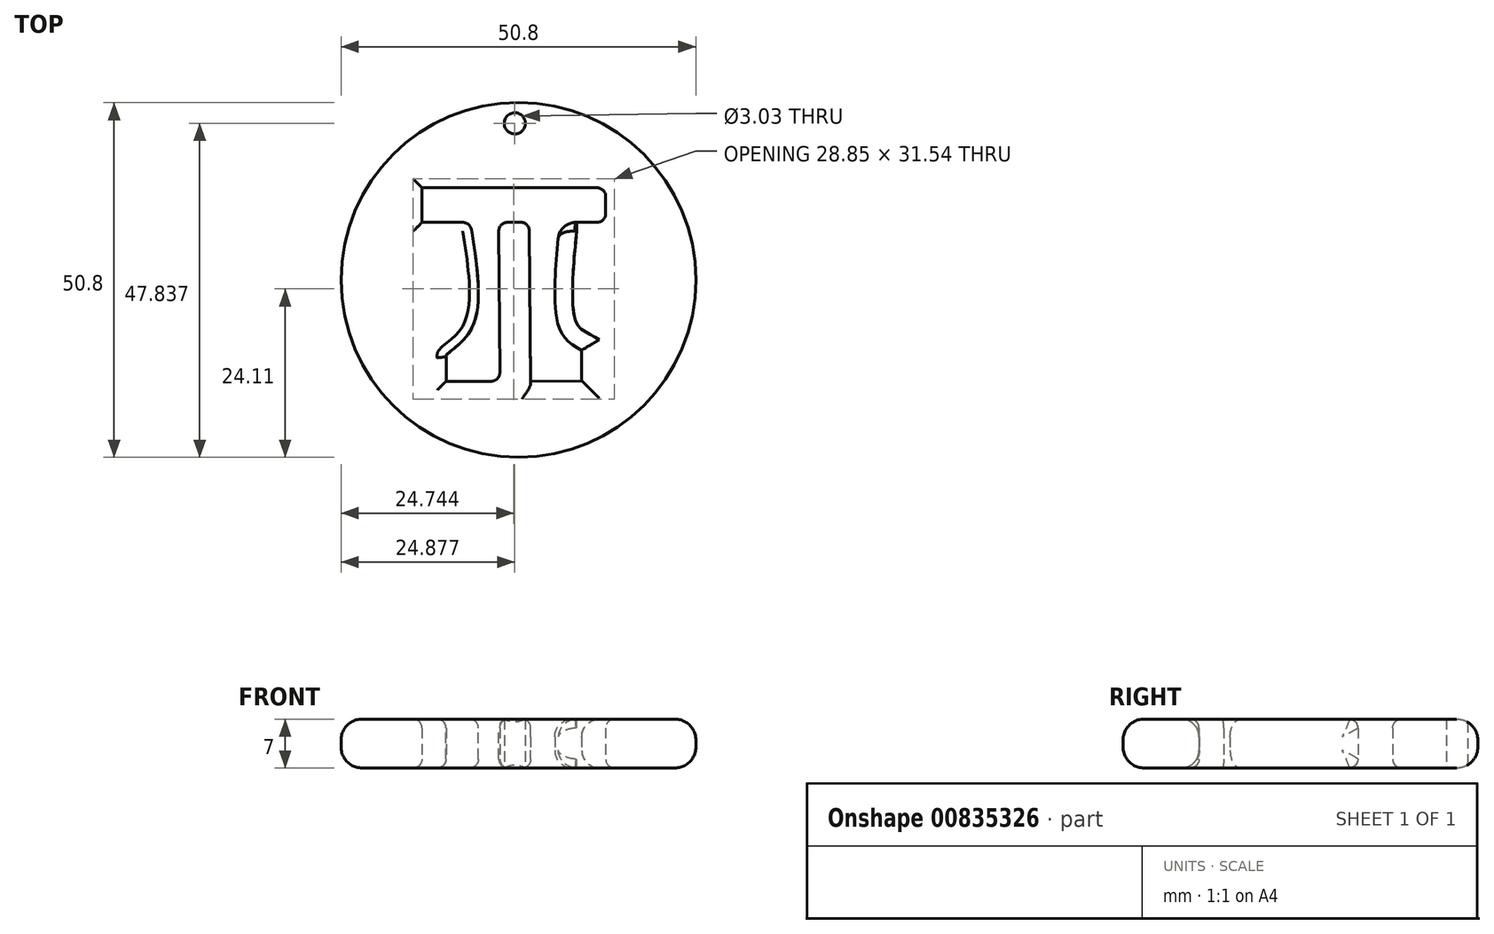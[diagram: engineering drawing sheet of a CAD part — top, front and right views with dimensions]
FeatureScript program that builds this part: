
annotation { "Feature Type Name" : "Feature", "Feature Type Description" : "" }
export const myFeature = defineFeature(function(context is Context, id is Id, definition is map)
    precondition{}
    {
        {
            var Q0;
            Q0=qCreatedBy(makeId("Top.planeOp"),FACE);
            var sketch = newSketch(context, id + "F0", { "sketchPlane" : qUnion([Q0])});
            skLineSegment(sketch, "E0", {"start": v(-26.31, 22.35) * mm, "end": v(0, 22.35) * mm});
            skLineSegment(sketch, "E1", {"start": v(0, 22.35) * mm, "end": v(0, 17.38) * mm});
            skLineSegment(sketch, "E2", {"start": v(0, 17.38) * mm, "end": v(-4.14, 17.38) * mm});
            skLineSegment(sketch, "E3", {"start": v(-26.31, 22.35) * mm, "end": v(-26.31, 17.38) * mm});
            skLineSegment(sketch, "E4", {"start": v(-26.31, 17.38) * mm, "end": v(-19.4, 17.38) * mm});
            skLineSegment(sketch, "E5", {"start": v(0, 17.38) * mm, "end": v(0, 19.87) * mm});
            skPoint(sketch, "E6.2.internal.snap0", {"position": v(-22.86, 17.38) * mm});
            skPoint(sketch, "E6.3.internal.snap0", {"position": v(-22.86, 17.38) * mm});
            skFitSpline(sketch, "E6", {"points": [v(-19.4, 17.38) * mm, v(-19.4, 1.83) * mm, v(-22.86, -1.63) * mm, v(-22.86, -1.83) * mm], "startDerivative": vector(5.13, -31.3) * mm, "endDerivative": vector(1.12, -2.6) * mm});
            skLineSegment(sketch, "E7", {"start": v(-22.86, -1.63) * mm, "end": v(-22.86, -5.37) * mm});
            skLineSegment(sketch, "E8", {"start": v(-22.86, -5.37) * mm, "end": v(-15.14, -5.37) * mm});
            skLineSegment(sketch, "E9", {"start": v(-15.34, 17.38) * mm, "end": v(-15.14, -5.37) * mm});
            skPoint(sketch, "E9.startSnap0", {"position": v(-2.07, 17.38) * mm});
            skLineSegment(sketch, "E10", {"start": v(-15.34, 17.38) * mm, "end": v(-10.94, 17.42) * mm});
            skLineSegment(sketch, "E11", {"start": v(-10.94, 17.42) * mm, "end": v(-10.75, -5.37) * mm});
            skCircle(sketch, "E12", {"center": v(-12.5, 9.14) * mm, "radius": 25.4 * mm});
            skCircle(sketch, "E13", {"center": v(-13.02, 31.58) * mm, "radius": 1.52 * mm});
            skCircle(sketch, "E14", {"center": v(-13.02, 31.58) * mm, "radius": 1.4 * mm});
            skLineSegment(sketch, "E15", {"start": v(-10.75, -5.37) * mm, "end": v(-3.43, -5.3) * mm});
            skLineSegment(sketch, "E16", {"start": v(-4.14, 17.38) * mm, "end": v(-5.38, 17.38) * mm});
            skLineSegment(sketch, "E17", {"start": v(-5.38, 17.38) * mm, "end": v(-6.56, 17.38) * mm});
            skFitSpline(sketch, "E18", {"points": [v(-6.56, 17.38) * mm, v(-6.56, 2.02) * mm, v(-3.43, -0.92) * mm], "startDerivative": vector(-3.15, -28.69) * mm, "endDerivative": vector(11.53, -6.13) * mm});
            skLineSegment(sketch, "E19", {"start": v(-3.43, -0.92) * mm, "end": v(-3.43, -5.3) * mm});
            skSolve(sketch);
        }
        {
            var Q0;
            Q0 = qSketchRegion(id + "F0", true);
            extrude(context, id + "F1", {"entities" : qUnion([Q0]), "depth" : 7 * mm, "offsetDistance" : 25.4 * mm});
        }
        {
            var Q0;
            Q0 = qSketchRegion(id + "F0", true);
            extrude(context, id + "F2", {"entities" : qUnion([Q0]), "operationType" : NewBodyOperationType.ADD, "depth" : 7 * mm, "offsetDistance" : 25.4 * mm});
        }
        {
            var Q0;
            Q0=makeQuery(id+"F1.opExtrude","CAP_EDGE",EDGE,{"disambiguationData":[OSD([sQuery(id+"F0.wireOp",EDGE,"E12")])],"isStart":false});
            var Q1;
            Q1=makeQuery(id+"F1.opExtrude","CAP_EDGE",EDGE,{"disambiguationData":[OSD([sQuery(id+"F0.wireOp",EDGE,"E12")])],"isStart":true});
            fillet(context, id + "F3", {"entities" : qUnion([Q0, Q1]), "radius" : 3 * mm, "tangentPropagation" : true, "allowEdgeOverflow" : false});
        }
        {
            var Q0;
            Q0=makeQuery(id+"F1.opExtrude","CAP_EDGE",EDGE,{"disambiguationData":[OSD([sQuery(id+"F0.wireOp",EDGE,"E6")])],"isStart":false});
            var Q1;
            Q1=makeQuery(id+"F1.opExtrude","CAP_EDGE",EDGE,{"disambiguationData":[OSD([sQuery(id+"F0.wireOp",EDGE,"E9")])],"isStart":false});
            var Q2;
            Q2=makeQuery(id+"F1.opExtrude","CAP_EDGE",EDGE,{"disambiguationData":[OSD([sQuery(id+"F0.wireOp",EDGE,"E7")])],"isStart":false});
            var Q3;
            Q3=makeQuery(id+"F1.opExtrude","CAP_EDGE",EDGE,{"disambiguationData":[OSD([sQuery(id+"F0.wireOp",EDGE,"E8")])],"isStart":false});
            var Q4;
            Q4=makeQuery(id+"F1.opExtrude","CAP_EDGE",EDGE,{"disambiguationData":[OSD([sQuery(id+"F0.wireOp",EDGE,"E3")])],"isStart":false});
            var Q5;
            Q5=makeQuery(id+"F1.opExtrude","CAP_EDGE",EDGE,{"disambiguationData":[OSD([sQuery(id+"F0.wireOp",EDGE,"E4")])],"isStart":false});
            var Q6;
            Q6=makeQuery(id+"F1.opExtrude","CAP_EDGE",EDGE,{"disambiguationData":[OSD([sQuery(id+"F0.wireOp",EDGE,"E0")])],"isStart":false});
            var Q7;
            Q7=makeQuery(id+"F1.opExtrude","CAP_EDGE",EDGE,{"disambiguationData":[OSD([sQuery(id+"F0.wireOp",EDGE,"E11")])],"isStart":false});
            var Q8;
            Q8=makeQuery(id+"F1.opExtrude","CAP_EDGE",EDGE,{"disambiguationData":[OSD([sQuery(id+"F0.wireOp",EDGE,"E10")])],"isStart":false});
            var Q9;
            Q9=makeQuery(id+"F1.opExtrude","CAP_EDGE",EDGE,{"disambiguationData":[OSD([sQuery(id+"F0.wireOp",EDGE,"542dcd29-0e0e-4ffc-a410-014b1dc8fc08")])],"isStart":false});
            var Q10;
            Q10=makeQuery(id+"F1.opExtrude","CAP_EDGE",EDGE,{"disambiguationData":[OSD([sQuery(id+"F0.wireOp",EDGE,"FAmDEnbx-qt7p-qUkV-MvWz-SRrdRzNlyzaC")])],"isStart":false});
            var Q11;
            Q11=makeQuery(id+"F1.opExtrude","CAP_EDGE",EDGE,{"disambiguationData":[OSD([sQuery(id+"F0.wireOp",EDGE,"VQDaXQRg-7JFO-pH3q-cyT9-IfhUXavPjLha"),sQuery(id+"F0.wireOp",EDGE,"Oee3kpTU-0iA1-8aof-Phc5-YmfvFTmY5mBl")])],"isStart":false});
            var Q12;
            Q12=makeQuery(id+"F1.opExtrude","CAP_EDGE",EDGE,{"disambiguationData":[OSD([sQuery(id+"F0.wireOp",EDGE,"E2")])],"isStart":false});
            var Q13;
            Q13=makeQuery(id+"F1.opExtrude","CAP_EDGE",EDGE,{"disambiguationData":[OSD([sQuery(id+"F0.wireOp",EDGE,"E1"),sQuery(id+"F0.wireOp",EDGE,"E5")])],"isStart":false});
            var Q14;
            Q14=makeQuery(id+"F1.opExtrude","CAP_EDGE",EDGE,{"disambiguationData":[OSD([sQuery(id+"F0.wireOp",EDGE,"E1"),sQuery(id+"F0.wireOp",EDGE,"E5")])],"isStart":true});
            var Q15;
            Q15=makeQuery(id+"F1.opExtrude","CAP_EDGE",EDGE,{"disambiguationData":[OSD([sQuery(id+"F0.wireOp",EDGE,"E0")])],"isStart":true});
            var Q16;
            Q16=makeQuery(id+"F1.opExtrude","SWEPT_EDGE",EDGE,{"disambiguationData":[OSD([sQuery(id+"F0.wireOp",EDGE,"E0"),sQuery(id+"F0.wireOp",EDGE,"E1")])]});
            var Q17;
            Q17=makeQuery(id+"F1.opExtrude","CAP_EDGE",EDGE,{"disambiguationData":[OSD([sQuery(id+"F0.wireOp",EDGE,"E2")])],"isStart":true});
            var Q18;
            Q18=makeQuery(id+"F1.opExtrude","CAP_EDGE",EDGE,{"disambiguationData":[OSD([sQuery(id+"F0.wireOp",EDGE,"542dcd29-0e0e-4ffc-a410-014b1dc8fc08")])],"isStart":true});
            var Q19;
            Q19=makeQuery(id+"F1.opExtrude","CAP_EDGE",EDGE,{"disambiguationData":[OSD([sQuery(id+"F0.wireOp",EDGE,"FAmDEnbx-qt7p-qUkV-MvWz-SRrdRzNlyzaC")])],"isStart":true});
            var Q20;
            Q20=makeQuery(id+"F1.opExtrude","CAP_EDGE",EDGE,{"disambiguationData":[OSD([sQuery(id+"F0.wireOp",EDGE,"VQDaXQRg-7JFO-pH3q-cyT9-IfhUXavPjLha"),sQuery(id+"F0.wireOp",EDGE,"Oee3kpTU-0iA1-8aof-Phc5-YmfvFTmY5mBl")])],"isStart":true});
            var Q21;
            Q21=makeQuery(id+"F1.opExtrude","SWEPT_EDGE",EDGE,{"disambiguationData":[OSD([sQuery(id+"F0.wireOp",EDGE,"542dcd29-0e0e-4ffc-a410-014b1dc8fc08"),sQuery(id+"F0.wireOp",EDGE,"FAmDEnbx-qt7p-qUkV-MvWz-SRrdRzNlyzaC")])]});
            var Q22;
            Q22=makeQuery(id+"F1.opExtrude","CAP_EDGE",EDGE,{"disambiguationData":[OSD([sQuery(id+"F0.wireOp",EDGE,"E11")])],"isStart":true});
            var Q23;
            Q23=makeQuery(id+"F1.opExtrude","CAP_EDGE",EDGE,{"disambiguationData":[OSD([sQuery(id+"F0.wireOp",EDGE,"E4")])],"isStart":true});
            var Q24;
            Q24=makeQuery(id+"F1.opExtrude","CAP_EDGE",EDGE,{"disambiguationData":[OSD([sQuery(id+"F0.wireOp",EDGE,"E6")])],"isStart":true});
            var Q25;
            Q25=makeQuery(id+"F1.opExtrude","CAP_EDGE",EDGE,{"disambiguationData":[OSD([sQuery(id+"F0.wireOp",EDGE,"E3")])],"isStart":true});
            var Q26;
            Q26=makeQuery(id+"F1.opExtrude","SWEPT_FACE",FACE,{"disambiguationData":[OSD([sQuery(id+"F0.wireOp",EDGE,"E9")])]});
            var Q27;
            Q27=makeQuery(id+"F1.opExtrude","CAP_EDGE",EDGE,{"disambiguationData":[OSD([sQuery(id+"F0.wireOp",EDGE,"E10")])],"isStart":true});
            var Q28;
            Q28=makeQuery(id+"F1.opExtrude","CAP_EDGE",EDGE,{"disambiguationData":[OSD([sQuery(id+"F0.wireOp",EDGE,"E8")])],"isStart":true});
            var Q29;
            Q29=makeQuery(id+"F1.opExtrude","CAP_EDGE",EDGE,{"disambiguationData":[OSD([sQuery(id+"F0.wireOp",EDGE,"E7")])],"isStart":true});
            var Q30;
            Q30=makeQuery(id+"F1.opExtrude","SWEPT_EDGE",EDGE,{"disambiguationData":[OSD([sQuery(id+"F0.wireOp",EDGE,"E10"),sQuery(id+"F0.wireOp",EDGE,"E11")])]});
            var Q31;
            Q31=makeQuery(id+"F1.opExtrude","SWEPT_EDGE",EDGE,{"disambiguationData":[OSD([sQuery(id+"F0.wireOp",EDGE,"E2"),sQuery(id+"F0.wireOp",EDGE,"542dcd29-0e0e-4ffc-a410-014b1dc8fc08")])]});
            var Q32;
            Q32=makeQuery(id+"F1.opExtrude","SWEPT_EDGE",EDGE,{"disambiguationData":[OSD([sQuery(id+"F0.wireOp",EDGE,"E4"),sQuery(id+"F0.wireOp",EDGE,"E6")])]});
            fillet(context, id + "F4", {"entities" : qUnion([Q0, Q1, Q2, Q3, Q4, Q5, Q6, Q7, Q8, Q9, Q10, Q11, Q12, Q13, Q14, Q15, Q16, Q17, Q18, Q19, Q20, Q21, Q22, Q23, Q24, Q25, Q26, Q27, Q28, Q29, Q30, Q31, Q32]), "radius" : 1.27 * mm, "tangentPropagation" : true, "allowEdgeOverflow" : false});
        }
        {
            var Q0;
            Q0=makeQuery(id+"F1.opExtrude","CAP_EDGE",EDGE,{"disambiguationData":[OSD([sQuery(id+"F0.wireOp",EDGE,"E18")])],"isStart":false});
            var Q1;
            Q1=makeQuery(id+"F1.opExtrude","CAP_EDGE",EDGE,{"disambiguationData":[OSD([sQuery(id+"F0.wireOp",EDGE,"E19")])],"isStart":false});
            var Q2;
            Q2=makeQuery(id+"F1.opExtrude","CAP_EDGE",EDGE,{"disambiguationData":[OSD([sQuery(id+"F0.wireOp",EDGE,"E15")])],"isStart":false});
            var Q3;
            Q3=makeQuery(id+"F1.opExtrude","CAP_EDGE",EDGE,{"disambiguationData":[OSD([sQuery(id+"F0.wireOp",EDGE,"E19")])],"isStart":true});
            var Q4;
            Q4=makeQuery(id+"F1.opExtrude","CAP_EDGE",EDGE,{"disambiguationData":[OSD([sQuery(id+"F0.wireOp",EDGE,"E15")])],"isStart":true});
            fillet(context, id + "F5", {"entities" : qUnion([Q0, Q1, Q2, Q3, Q4]), "radius" : 2.54 * mm, "tangentPropagation" : true, "allowEdgeOverflow" : false});
        }
    });
